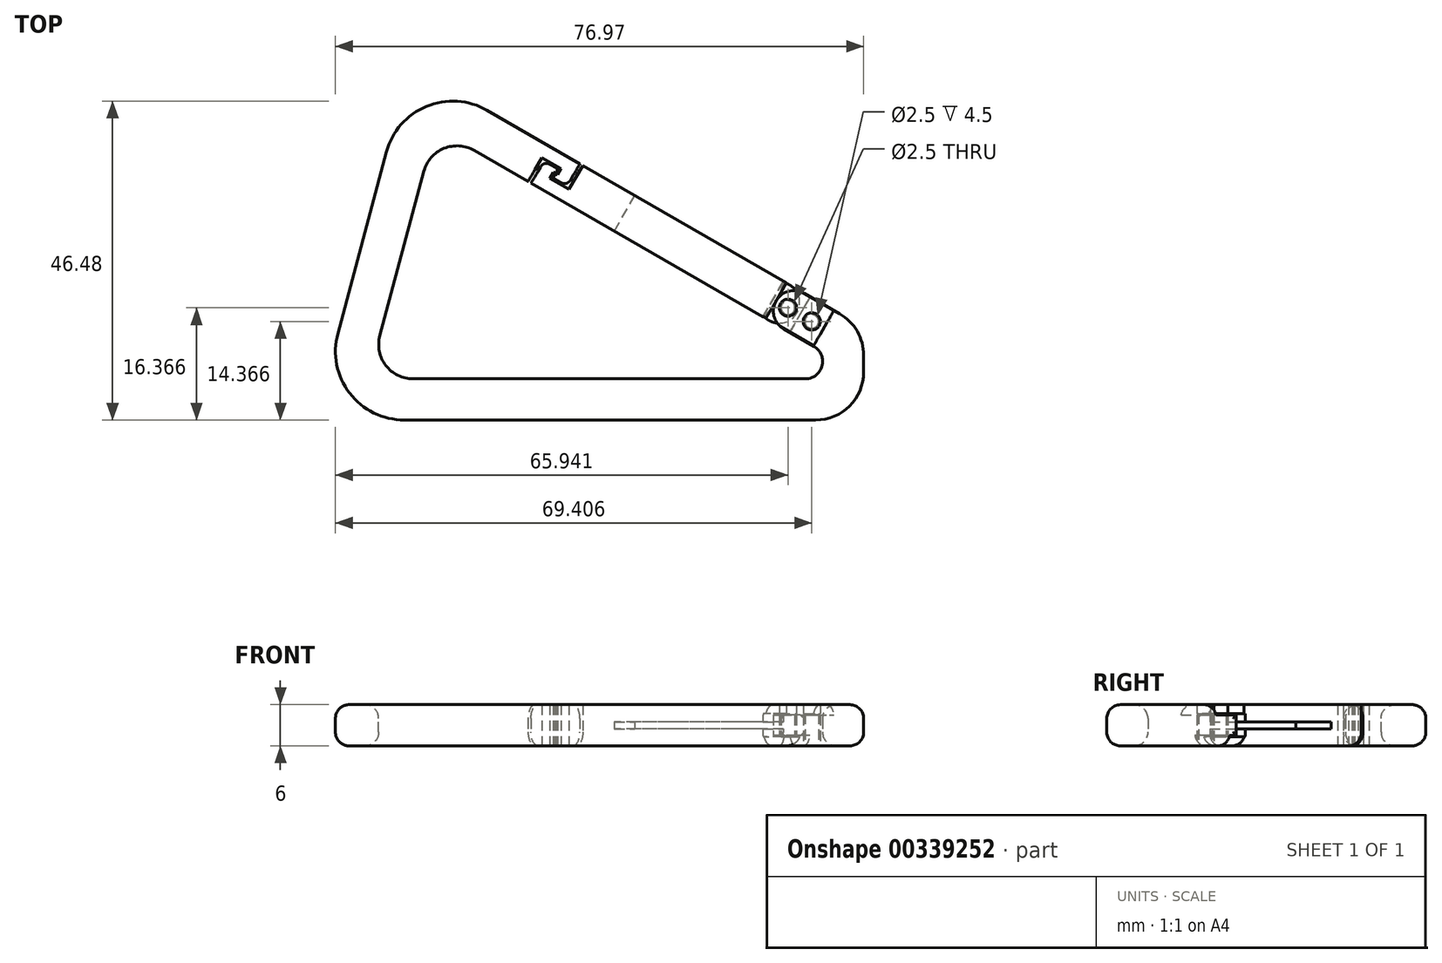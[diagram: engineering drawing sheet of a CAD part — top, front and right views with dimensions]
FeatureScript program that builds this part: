
annotation { "Feature Type Name" : "Feature", "Feature Type Description" : "" }
export const myFeature = defineFeature(function(context is Context, id is Id, definition is map)
    precondition{}
    {
        {
            var Q0;
            Q0=qCreatedBy(makeId("Top.planeOp"),FACE);
            var sketch = newSketch(context, id + "F0", { "sketchPlane" : qUnion([Q0])});
            skLineSegment(sketch, "E0", {"start": v(-37.94, 0) * mm, "end": v(42.06, 0) * mm});
            skLineSegment(sketch, "E1", {"start": v(42.06, 0) * mm, "end": v(42.06, 13.46) * mm});
            skLineSegment(sketch, "E2", {"start": v(42.06, 13.46) * mm, "end": v(30.8, 19.96) * mm});
            skLineSegment(sketch, "E3", {"start": v(-37.94, 0) * mm, "end": v(-24.1, 51.66) * mm});
            skLineSegment(sketch, "E4", {"start": v(-24.1, 51.66) * mm, "end": v(-3.84, 39.96) * mm});
            skLineSegment(sketch, "E5", {"start": v(-3.84, 39.96) * mm, "end": v(-6.84, 34.77) * mm});
            skLineSegment(sketch, "E6", {"start": v(-6.84, 34.77) * mm, "end": v(-20.33, 42.55) * mm});
            skLineSegment(sketch, "E7", {"start": v(-20.33, 42.55) * mm, "end": v(-30.12, 6) * mm});
            skLineSegment(sketch, "E8", {"start": v(-30.12, 6) * mm, "end": v(36.06, 6) * mm});
            skLineSegment(sketch, "E9", {"start": v(36.06, 6) * mm, "end": v(36.06, 6) * mm});
            skLineSegment(sketch, "E10", {"start": v(36.06, 6) * mm, "end": v(36.06, 10) * mm});
            skLineSegment(sketch, "E11", {"start": v(36.06, 10) * mm, "end": v(27.8, 14.77) * mm});
            skLineSegment(sketch, "E12", {"start": v(27.8, 14.77) * mm, "end": v(30.8, 19.96) * mm});
            skLineSegment(sketch, "E13", {"start": v(69.38, 0) * mm, "end": v(-54.64, 71.6) * mm, "construction": true});
            skLineSegment(sketch, "E14", {"start": v(-7.01, 41.8) * mm, "end": v(0.7, 37.34) * mm});
            skLineSegment(sketch, "E15", {"start": v(0.7, 37.34) * mm, "end": v(-1.17, 34.1) * mm});
            skLineSegment(sketch, "E16", {"start": v(-1.17, 34.1) * mm, "end": v(-2.9, 35.1) * mm});
            skLineSegment(sketch, "E17", {"start": v(-2.9, 35.1) * mm, "end": v(-2.9, 35.1) * mm});
            skLineSegment(sketch, "E18", {"start": v(-2.9, 35.1) * mm, "end": v(-2.03, 36.6) * mm});
            skLineSegment(sketch, "E19", {"start": v(-2.03, 36.6) * mm, "end": v(-4.84, 38.23) * mm});
            skLineSegment(sketch, "E20", {"start": v(-16.76, 43.96) * mm, "end": v(37.05, 12.89) * mm, "construction": true});
            skLineSegment(sketch, "E21", {"start": v(26.2, 15.7) * mm, "end": v(-6.4, 34.52) * mm});
            skLineSegment(sketch, "E22", {"start": v(-6.4, 34.52) * mm, "end": v(-4.53, 37.77) * mm});
            skLineSegment(sketch, "E23", {"start": v(-4.53, 37.77) * mm, "end": v(-4.53, 37.77) * mm});
            skLineSegment(sketch, "E24", {"start": v(-4.53, 37.77) * mm, "end": v(-2.8, 36.77) * mm});
            skLineSegment(sketch, "E25", {"start": v(-2.8, 36.77) * mm, "end": v(-3.68, 35.25) * mm});
            skLineSegment(sketch, "E26", {"start": v(-3.68, 35.25) * mm, "end": v(-0.86, 33.62) * mm});
            skLineSegment(sketch, "E27", {"start": v(-0.86, 33.62) * mm, "end": v(1.14, 37.09) * mm});
            skLineSegment(sketch, "E28", {"start": v(1.14, 37.09) * mm, "end": v(30.37, 20.21) * mm});
            skLineSegment(sketch, "E29", {"start": v(30.37, 20.21) * mm, "end": v(27.37, 15.02) * mm});
            skLineSegment(sketch, "E30", {"start": v(27.37, 15.02) * mm, "end": v(26.2, 15.7) * mm});
            skLineSegment(sketch, "E31", {"start": v(34.26, 17.96) * mm, "end": v(31.26, 12.77) * mm});
            skLineSegment(sketch, "E32", {"start": v(34.73, 10.77) * mm, "end": v(37.73, 15.96) * mm});
            skCircle(sketch, "E33", {"center": v(31.03, 16.37) * mm, "radius": 1.25 * mm});
            skCircle(sketch, "E34", {"center": v(34.5, 14.37) * mm, "radius": 1.25 * mm});
            skCircle(sketch, "E35", {"center": v(31.03, 16.37) * mm, "radius": 1 * mm});
            skCircle(sketch, "E36", {"center": v(34.5, 14.37) * mm, "radius": 1 * mm});
            skLineSegment(sketch, "E37", {"start": v(-2.87, 35.94) * mm, "end": v(-2.53, 35.74) * mm});
            skLineSegment(sketch, "E38", {"start": v(-2.8, 36.77) * mm, "end": v(-2.46, 36.57) * mm});
            skLineSegment(sketch, "E39", {"start": v(-2.46, 36.57) * mm, "end": v(-2.83, 35.92) * mm});
            skLineSegment(sketch, "E40", {"start": v(-2.83, 35.92) * mm, "end": v(-3.18, 36.12) * mm});
            skLineSegment(sketch, "E41", {"start": v(-2.9, 35.1) * mm, "end": v(-3.26, 35.3) * mm});
            skLineSegment(sketch, "E42", {"start": v(-3.26, 35.3) * mm, "end": v(-2.87, 35.94) * mm});
            skSolve(sketch);
        }
        {
            var Q0;
            Q0=makeQuery(id+"F0.imprint","IMPRINT",FACE,{"disambiguationData":[TD([[makeQuery(id+"F0.imprint","IMPRINT",EDGE,{"derivedFrom":sQuery(id+"F0.wireOp",EDGE,"E0")}),1.0]])]});
            var Q1;
            {var subQ4=sQuery(id+"F0.wireOp",EDGE,"E15");Q1=makeQuery(id+"F0.imprint","IMPRINT",FACE,{"disambiguationData":[TD([[makeQuery(id+"F0.imprint","IMPRINT",EDGE,{"derivedFrom":subQ4}),-1.0]])]});}
            var Q2;
            {var subQ0=sQuery(id+"F0.wireOp",EDGE,"E31");Q2=makeQuery(id+"F0.imprint","IMPRINT",FACE,{"disambiguationData":[TD([[makeQuery(id+"F0.imprint","IMPRINT",EDGE,{"derivedFrom":subQ0}),1.0]])]});}
            var Q3;
            {var subQ0=sQuery(id+"F0.wireOp",EDGE,"E12");Q3=makeQuery(id+"F0.imprint","IMPRINT",FACE,{"disambiguationData":[TD([[makeQuery(id+"F0.imprint","IMPRINT",EDGE,{"derivedFrom":subQ0}),-1.0]])]});}
            var Q4;
            {var subQ0=sQuery(id+"F0.wireOp",EDGE,"dfad1d2e-a19c-48b1-9bc2-72230bd4c4e1");Q4=makeQuery(id+"F0.imprint","IMPRINT",FACE,{"disambiguationData":[TD([[makeQuery(id+"F0.imprint","IMPRINT",EDGE,{"derivedFrom":subQ0}),-1.0]])]});}
            var Q5;
            {var subQ1=sQuery(id+"F0.wireOp",EDGE,"E37");Q5=makeQuery(id+"F0.imprint","IMPRINT",FACE,{"disambiguationData":[TD([[makeQuery(id+"F0.imprint","IMPRINT",EDGE,{"derivedFrom":subQ1}),-1.0]])]});}
            extrude(context, id + "F1", {"entities" : qUnion([Q0, Q1, Q2, Q3, Q4, Q5]), "depth" : 6 * mm});
        }
        {
            var Q0;
            Q0=makeQuery(id+"F1.opExtrude","SWEPT_EDGE",EDGE,{"disambiguationData":[OSD([sQuery(id+"F0.wireOp",EDGE,"E0"),sQuery(id+"F0.wireOp",EDGE,"E3")])]});
            var Q1;
            Q1=makeQuery(id+"F1.opExtrude","SWEPT_EDGE",EDGE,{"disambiguationData":[OSD([sQuery(id+"F0.wireOp",EDGE,"E3"),sQuery(id+"F0.wireOp",EDGE,"E4")])]});
            fillet(context, id + "F2", {"entities" : qUnion([Q0, Q1]), "radius" : 10 * mm, "tangentPropagation" : true, "allowEdgeOverflow" : false});
        }
        {
            var Q0;
            Q0=makeQuery(id+"F1.opExtrude","SWEPT_EDGE",EDGE,{"disambiguationData":[OSD([sQuery(id+"F0.wireOp",EDGE,"E1"),sQuery(id+"F0.wireOp",EDGE,"E2")])]});
            var Q1;
            Q1=makeQuery(id+"F1.opExtrude","SWEPT_EDGE",EDGE,{"disambiguationData":[OSD([sQuery(id+"F0.wireOp",EDGE,"E0"),sQuery(id+"F0.wireOp",EDGE,"E1")])]});
            fillet(context, id + "F3", {"entities" : qUnion([Q0, Q1]), "radius" : 7 * mm, "tangentPropagation" : true, "allowEdgeOverflow" : false});
        }
        {
            var Q0;
            Q0=makeQuery(id+"F1.opExtrude","SWEPT_EDGE",EDGE,{"disambiguationData":[OSD([sQuery(id+"F0.wireOp",EDGE,"E10"),sQuery(id+"F0.wireOp",EDGE,"E11")])]});
            var Q1;
            Q1=makeQuery(id+"F1.opExtrude","SWEPT_EDGE",EDGE,{"disambiguationData":[OSD([sQuery(id+"F0.wireOp",EDGE,"E8"),sQuery(id+"F0.wireOp",EDGE,"E10")])]});
            fillet(context, id + "F4", {"entities" : qUnion([Q0, Q1]), "radius" : 2.5 * mm, "tangentPropagation" : true, "allowEdgeOverflow" : false});
        }
        {
            var Q0;
            Q0=makeQuery(id+"F1.opExtrude","SWEPT_EDGE",EDGE,{"disambiguationData":[OSD([sQuery(id+"F0.wireOp",EDGE,"E7"),sQuery(id+"F0.wireOp",EDGE,"E8")])]});
            var Q1;
            Q1=makeQuery(id+"F1.opExtrude","SWEPT_EDGE",EDGE,{"disambiguationData":[OSD([sQuery(id+"F0.wireOp",EDGE,"E6"),sQuery(id+"F0.wireOp",EDGE,"E7")])]});
            fillet(context, id + "F5", {"entities" : qUnion([Q0, Q1]), "radius" : 5 * mm, "tangentPropagation" : true, "allowEdgeOverflow" : false});
        }
        {
            var Q0;
            {var subQ0=sQuery(id+"F0.wireOp",EDGE,"E12");Q0=makeQuery(id+"F0.imprint","IMPRINT",FACE,{"disambiguationData":[TD([[makeQuery(id+"F0.imprint","IMPRINT",EDGE,{"derivedFrom":subQ0}),-1.0]])]});}
            extrude(context, id + "F6", {"entities" : qUnion([Q0]), "operationType" : NewBodyOperationType.REMOVE, "depth" : 1.5 * mm});
        }
        {
            var Q0;
            Q0=makeQuery(id+"F0.imprint","IMPRINT",FACE,{"disambiguationData":[TD([[makeQuery(id+"F0.imprint","IMPRINT",EDGE,{"derivedFrom":sQuery(id+"F0.wireOp",EDGE,"E21")}),-1.0]])]});
            var Q1;
            {var subQ0=sQuery(id+"F0.wireOp",EDGE,"E38");Q1=makeQuery(id+"F0.imprint","IMPRINT",FACE,{"disambiguationData":[TD([[makeQuery(id+"F0.imprint","IMPRINT",EDGE,{"derivedFrom":subQ0}),-1.0]])]});}
            extrude(context, id + "F7", {"entities" : qUnion([Q0, Q1]), "depth" : 6 * mm});
        }
        {
            var Q0;
            Q0=makeQuery(id+"F7.opExtrude","SWEPT_FACE",FACE,{"disambiguationData":[OSD([sQuery(id+"F0.wireOp",EDGE,"E29")])]});
            var sketch = newSketch(context, id + "F8", { "sketchPlane" : qUnion([Q0])});
            skLineSegment(sketch, "E43", {"start": v(32.69, 4.7) * mm, "end": v(26.69, 4.7) * mm});
            skLineSegment(sketch, "E44", {"start": v(32.69, 1.3) * mm, "end": v(26.69, 1.3) * mm});
            skLineSegment(sketch, "E45", {"start": v(32.69, 4.7) * mm, "end": v(32.69, 6) * mm});
            skLineSegment(sketch, "E46", {"start": v(32.69, 6) * mm, "end": v(26.69, 6) * mm});
            skLineSegment(sketch, "E47", {"start": v(26.69, 6) * mm, "end": v(26.69, 4.7) * mm});
            skLineSegment(sketch, "E48", {"start": v(26.69, 1.3) * mm, "end": v(26.69, 0) * mm});
            skLineSegment(sketch, "E49", {"start": v(26.69, 0) * mm, "end": v(32.69, 0) * mm});
            skLineSegment(sketch, "E50", {"start": v(32.69, 0) * mm, "end": v(32.69, 1.3) * mm});
            skLineSegment(sketch, "E51", {"start": v(26.69, 4.7) * mm, "end": v(26.19, 4.7) * mm});
            skLineSegment(sketch, "E52", {"start": v(26.19, 4.7) * mm, "end": v(26.19, 1.3) * mm});
            skLineSegment(sketch, "E53", {"start": v(26.19, 1.3) * mm, "end": v(26.69, 1.3) * mm});
            skLineSegment(sketch, "E54", {"start": v(26.69, 4.7) * mm, "end": v(26.69, 1.3) * mm});
            skLineSegment(sketch, "E55", {"start": v(26.19, 4.7) * mm, "end": v(26.19, 6) * mm});
            skLineSegment(sketch, "E56", {"start": v(26.19, 6) * mm, "end": v(26.69, 6) * mm});
            skLineSegment(sketch, "E57", {"start": v(26.69, 0) * mm, "end": v(26.18, 0) * mm});
            skLineSegment(sketch, "E58", {"start": v(26.18, 0) * mm, "end": v(26.19, 1.3) * mm});
            skSolve(sketch);
        }
        {
            var Q0;
            Q0=makeQuery(id+"F8.imprint","IMPRINT",FACE,{"disambiguationData":[TD([[makeQuery(id+"F8.imprint","IMPRINT",EDGE,{"derivedFrom":sQuery(id+"F8.wireOp",EDGE,"E43")}),-1.0]])]});
            extrude(context, id + "F9", {"entities" : qUnion([Q0]), "operationType" : NewBodyOperationType.ADD, "depth" : 8 * mm});
        }
        {
            var Q0;
            Q0=makeQuery(id+"F8.imprint","IMPRINT",FACE,{"disambiguationData":[TD([[makeQuery(id+"F8.imprint","IMPRINT",EDGE,{"derivedFrom":sQuery(id+"F8.wireOp",EDGE,"E44")}),1.0]])]});
            extrude(context, id + "F10", {"entities" : qUnion([Q0]), "operationType" : NewBodyOperationType.ADD, "depth" : 4 * mm});
        }
        {
            var Q0;
            {var subQ0=sQuery(id+"F0.wireOp",EDGE,"E31");Q0=makeQuery(id+"F0.imprint","IMPRINT",FACE,{"disambiguationData":[TD([[makeQuery(id+"F0.imprint","IMPRINT",EDGE,{"derivedFrom":subQ0}),1.0]])]});}
            var Q1;
            {var subQ0=sQuery(id+"F0.wireOp",EDGE,"E12");Q1=makeQuery(id+"F0.imprint","IMPRINT",FACE,{"disambiguationData":[TD([[makeQuery(id+"F0.imprint","IMPRINT",EDGE,{"derivedFrom":subQ0}),-1.0]])]});}
            extrude(context, id + "F11", {"entities" : qUnion([Q0, Q1]), "operationType" : NewBodyOperationType.REMOVE, "depth" : 6 * mm, "hasSecondDirection" : true, "secondDirectionOppositeDirection" : false, "secondDirectionDepth" : 4.5 * mm});
        }
        {
            var Q0;
            Q0=makeQuery(id+"F0.imprint","IMPRINT",FACE,{"disambiguationData":[TD([[makeQuery(id+"F0.imprint","IMPRINT",EDGE,{"derivedFrom":sQuery(id+"F0.wireOp",EDGE,"E36")}),1.0]])]});
            extrude(context, id + "F12", {"entities" : qUnion([Q0]), "operationType" : NewBodyOperationType.ADD, "depth" : 6 * mm});
        }
        {
            var Q0;
            Q0=makeQuery(id+"F0.imprint","IMPRINT",FACE,{"disambiguationData":[TD([[makeQuery(id+"F0.imprint","IMPRINT",EDGE,{"derivedFrom":sQuery(id+"F0.wireOp",EDGE,"E35")}),1.0]])]});
            extrude(context, id + "F13", {"entities" : qUnion([Q0]), "operationType" : NewBodyOperationType.ADD, "depth" : 4.5 * mm});
        }
        {
            var Q0;
            Q0=makeQuery(id+"F10.boolean.opBoolean","MERGE",FACE,{"derivedFrom":[makeQuery(id+"F9.boolean.opBoolean","MERGE",FACE,{"derivedFrom":[makeQuery(id+"F7.opExtrude","SWEPT_FACE",FACE,{"disambiguationData":[OSD([sQuery(id+"F0.wireOp",EDGE,"E28")])]}),makeQuery(id+"F9.opExtrude","SWEPT_FACE",FACE,{"disambiguationData":[OSD([sQuery(id+"F8.wireOp",EDGE,"E45")])]})]}),makeQuery(id+"F10.opExtrude","SWEPT_FACE",FACE,{"disambiguationData":[OSD([sQuery(id+"F8.wireOp",EDGE,"E50")])]})]});
            var sketch = newSketch(context, id + "F14", { "sketchPlane" : qUnion([Q0])});
            skLineSegment(sketch, "E59", {"start": v(-16.2, 3) * mm, "end": v(10.21, 3) * mm, "construction": true});
            skLineSegment(sketch, "E60.bottom", {"start": v(-16.2, 3.5) * mm, "end": v(8.8, 3.5) * mm});
            skLineSegment(sketch, "E60.top", {"start": v(-16.2, 2.5) * mm, "end": v(8.8, 2.5) * mm});
            skLineSegment(sketch, "E60.left", {"start": v(-16.2, 3.5) * mm, "end": v(-16.2, 2.5) * mm});
            skLineSegment(sketch, "E60.right", {"start": v(8.8, 3.5) * mm, "end": v(8.8, 2.5) * mm});
            skSolve(sketch);
        }
        {
            var Q0;
            Q0=makeQuery(id+"F14.imprint","IMPRINT",FACE,{"disambiguationData":[TD([[makeQuery(id+"F14.imprint","IMPRINT",EDGE,{"derivedFrom":sQuery(id+"F14.wireOp",EDGE,"E60.bottom")}),-1.0]])]});
            extrude(context, id + "F15", {"entities" : qUnion([Q0]), "operationType" : NewBodyOperationType.REMOVE, "oppositeDirection" : true, "depth" : 6 * mm});
        }
        {
            var Q0;
            Q0=makeQuery(id+"F1.opExtrude","CAP_EDGE",EDGE,{"disambiguationData":[OSD([sQuery(id+"F0.wireOp",EDGE,"E0")])],"isStart":false});
            var Q1;
            Q1=makeQuery(id+"F1.opExtrude","CAP_EDGE",EDGE,{"disambiguationData":[OSD([sQuery(id+"F0.wireOp",EDGE,"E0")])],"isStart":true});
            var Q2;
            Q2=makeQuery(id+"F1.opExtrude","CAP_EDGE",EDGE,{"disambiguationData":[OSD([sQuery(id+"F0.wireOp",EDGE,"E8")])],"isStart":true});
            var Q3;
            Q3=makeQuery(id+"F1.opExtrude","CAP_EDGE",EDGE,{"disambiguationData":[OSD([sQuery(id+"F0.wireOp",EDGE,"E7")])],"isStart":false});
            fillet(context, id + "F16", {"entities" : qUnion([Q0, Q1, Q2, Q3]), "radius" : 2 * mm, "tangentPropagation" : true, "allowEdgeOverflow" : false});
        }
        {
            var Q0;
            Q0=makeQuery(id+"F9.opExtrude","CAP_EDGE",EDGE,{"disambiguationData":[OSD([sQuery(id+"F8.wireOp",EDGE,"E45")])],"isStart":false});
            var Q1;
            Q1=makeQuery(id+"F10.opExtrude","CAP_EDGE",EDGE,{"disambiguationData":[OSD([sQuery(id+"F8.wireOp",EDGE,"E50")])],"isStart":false});
            var Q2;
            Q2=makeQuery(id+"F10.opExtrude","CAP_EDGE",EDGE,{"disambiguationData":[OSD([sQuery(id+"F8.wireOp",EDGE,"E48")])],"isStart":false});
            var Q3;
            Q3=makeQuery(id+"F9.opExtrude","CAP_EDGE",EDGE,{"disambiguationData":[OSD([sQuery(id+"F8.wireOp",EDGE,"E47")])],"isStart":false});
            fillet(context, id + "F17", {"entities" : qUnion([Q0, Q1, Q2, Q3]), "radius" : 3 * mm, "tangentPropagation" : true, "allowEdgeOverflow" : false});
        }
        {
            var Q0;
            Q0=makeQuery(id+"F1.opExtrude","SWEPT_EDGE",EDGE,{"disambiguationData":[OSD([sQuery(id+"F0.wireOp",EDGE,"E11"),sQuery(id+"F0.wireOp",EDGE,"E12")])]});
            var Q1;
            Q1=makeQuery(id+"F1.opExtrude","SWEPT_EDGE",EDGE,{"disambiguationData":[OSD([sQuery(id+"F0.wireOp",EDGE,"E2"),sQuery(id+"F0.wireOp",EDGE,"E12")])]});
            fillet(context, id + "F18", {"entities" : qUnion([Q0, Q1]), "radius" : 3 * mm, "tangentPropagation" : true, "allowEdgeOverflow" : false});
        }
        {
            var Q0;
            Q0=makeQuery(id+"F9.boolean.opBoolean","MERGE",EDGE,{"derivedFrom":[makeQuery(id+"F7.opExtrude","CAP_EDGE",EDGE,{"disambiguationData":[OSD([sQuery(id+"F0.wireOp",EDGE,"E21"),sQuery(id+"F0.wireOp",EDGE,"E30")])],"isStart":false}),makeQuery(id+"F9.opExtrude","SWEPT_EDGE",EDGE,{"disambiguationData":[OSD([sQuery(id+"F8.wireOp",EDGE,"E46"),sQuery(id+"F8.wireOp",EDGE,"E47"),sQuery(id+"F8.wireOp",EDGE,"E56")])]})]});
            var Q1;
            Q1=makeQuery(id+"F10.boolean.opBoolean","MERGE",EDGE,{"derivedFrom":[makeQuery(id+"F7.opExtrude","CAP_EDGE",EDGE,{"disambiguationData":[OSD([sQuery(id+"F0.wireOp",EDGE,"E21"),sQuery(id+"F0.wireOp",EDGE,"E30")])],"isStart":true}),makeQuery(id+"F10.opExtrude","SWEPT_EDGE",EDGE,{"disambiguationData":[OSD([sQuery(id+"F8.wireOp",EDGE,"E48"),sQuery(id+"F8.wireOp",EDGE,"E49"),sQuery(id+"F8.wireOp",EDGE,"E57")])]})]});
            fillet(context, id + "F19", {"entities" : qUnion([Q0, Q1]), "radius" : 2 * mm, "tangentPropagation" : true, "allowEdgeOverflow" : false});
        }
        {
            var Q0;
            Q0=makeQuery(id+"F1.opExtrude","SWEPT_EDGE",EDGE,{"disambiguationData":[OSD([sQuery(id+"F0.wireOp",EDGE,"E41"),sQuery(id+"F0.wireOp",EDGE,"E42")])]});
            var Q1;
            Q1=makeQuery(id+"F1.opExtrude","SWEPT_EDGE",EDGE,{"disambiguationData":[OSD([sQuery(id+"F0.wireOp",EDGE,"E40"),sQuery(id+"F0.wireOp",EDGE,"E42")])]});
            var Q2;
            Q2=makeQuery(id+"F7.opExtrude","SWEPT_EDGE",EDGE,{"disambiguationData":[OSD([sQuery(id+"F0.wireOp",EDGE,"E38"),sQuery(id+"F0.wireOp",EDGE,"E39")])]});
            var Q3;
            Q3=makeQuery(id+"F7.opExtrude","SWEPT_EDGE",EDGE,{"disambiguationData":[OSD([sQuery(id+"F0.wireOp",EDGE,"E37"),sQuery(id+"F0.wireOp",EDGE,"E39"),sQuery(id+"F0.wireOp",EDGE,"E40")])]});
            fillet(context, id + "F20", {"entities" : qUnion([Q0, Q1, Q2, Q3]), "radius" : 0.35 * mm, "tangentPropagation" : true, "allowEdgeOverflow" : false});
        }
        {
            var Q0;
            Q0=makeQuery(id+"F7.opExtrude","SWEPT_EDGE",EDGE,{"disambiguationData":[OSD([sQuery(id+"F0.wireOp",EDGE,"E22"),sQuery(id+"F0.wireOp",EDGE,"E24")])]});
            var Q1;
            Q1=makeQuery(id+"F1.opExtrude","SWEPT_EDGE",EDGE,{"disambiguationData":[OSD([sQuery(id+"F0.wireOp",EDGE,"E15"),sQuery(id+"F0.wireOp",EDGE,"E16")])]});
            fillet(context, id + "F21", {"entities" : qUnion([Q0, Q1]), "radius" : 1 * mm, "tangentPropagation" : true, "allowEdgeOverflow" : false});
        }
    });
